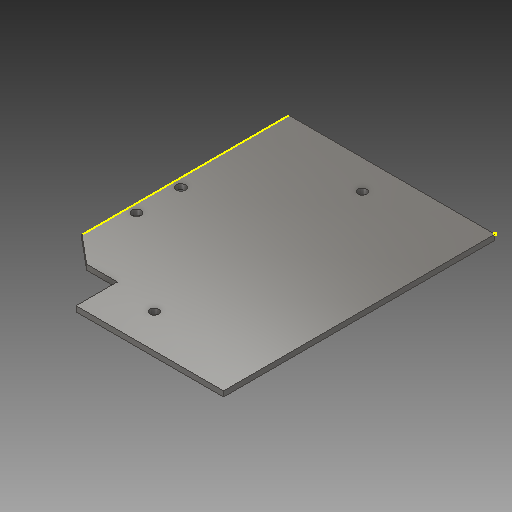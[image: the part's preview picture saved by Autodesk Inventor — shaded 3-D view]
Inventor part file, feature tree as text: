
AUTODESK INVENTOR PART (.ipt)
format: ipt  version: 2017 (Build 210142000, 142)  size: 110,592 bytes
history: native  units: in
note: dims shown in document units (in); Inventor stores cm internally (conversion verified against a paired STEP export)
features: other x3, sketch x3
ambient origin geometry x8: Origin, YZ Plane, XZ Plane, XY Plane, X Axis, Y Axis, Z Axis, Center Point
bodies: Solid1 (feature_tree)
feature tree (6):
  other  "flywheel plate.ipt"
  other  "Solid1::flywheel plate.ipt"
  other  "TaggingFeature1"
  sketch  "Sketch1"  dims[d0=0.3937in]
  sketch  "Sketch2"
  sketch  "Sketch3"
